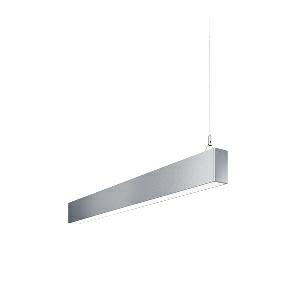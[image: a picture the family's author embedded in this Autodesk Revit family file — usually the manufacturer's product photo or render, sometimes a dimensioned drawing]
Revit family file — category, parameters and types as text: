
# Revit family: dotoo_line_-_dlp_1000_830_d_end_00805842_5508
name_source: partatom
category: Lighting Fixtures
units: mm (PartAtom-declared; Revit-internal decimal feet)

## family parameters
Cut with Voids When Loaded = No
Host = Face
Light Source = No
Part Type = Normal
Room Calculation Point = No
Round Connector Dimension = Use Diameter
Shared = No

## types (1)
- DOTOO.line - DLP 1000/830/D END (1 x LED, 1000 lm, 3000K)
    Apparent Load = 10 VA
    Approval mark = CE
    CIE Flux Codes = 67 91 98 100 100
    Color Rendering = 80-89
    Color Temperature = 3000K
    Control Gear = Electronic ballast
    Default Elevation = 1800 mm
    Description = DLP 1000/830/D|Suspended luminaire|light source: LED|connected load: 220-240 V, 50/60 Hz|Power consumption: approx. 10 W|standby: approx. 0,20|luminous flux: 1000 lm|luminous efficacy: 100 lm/W|light distribution: Direct|direct ratio: approx. 100 %|colour temperature: Warm white, ca. 3000 K|color rendering index (CRI): >= 80|chromaticity tolerance:  3 SDCM|System of protection: IP 40|technology: Continuously dimmable|luminaire body|material: Sectional aluminium|colour: Silver|lamp cover: Acrylic (PMMA), Clear|mains lead: 1,0 m With free stranded wires|Fastening: Steel cable 0.3 - 0.7 m|glare control: Prism aperture|luminance(L65): <= 3000 cd/m|unified glare rating(4H 8H): <=  19|special features: DALI Load 1x, TouchDIM - dimming via standard switch, Through-wired, up to 18 m on one mains connection, Flicker-free, Suitable as emergency lighting, Mechanical and electrical connection of the individual modules without tools|
    Frequency = 50 Hz
    Height = 110 mm
    Lamp = 1 x LED
    Lamp Light Flux = 1000 lm
    Lamp count = 1
    Length = 848 mm
    Luminous efficacy = 100 lm/W
    Manufacturer = Waldmann
    ModVariant = No
    Model = 00805842
    Mounting Place = Ceiling
    Mounting Type = Pendant
    Number of Poles = 1
    OnlyDefault = Yes
    Power Factor = 1
    Product Name = DOTOO.line - DLP 1000/830/D END
    Product group = Suspended luminaire
    ProductGroupID = 9
    Protection Class = Protection class I
    Protection Degree = IP 40
    RLX_Detail_Level = 1
    RLX_Emergency_Light_Flux = 0 lm
    RLX_Emergency_Type = 0
    RLX_Emergency_Type_DB = No
    RlxData = <blob elided: 18713 chars, md5=a484e0ee>
    Socket = socket
    Standby Power = 0 W
    System Light Flux = 1000 lm
    System Power = 10 W
    Type Comments = Product without accessories
    Type Image = 113300000-00692564.jpg
    URL = http://relux.com
    VarID = ---
    Voltage = 230 V
    Voltage Range = 220-240 V
    Weight = 0.00 kg
    Width = 60 mm  [stored 0.19685 ft]

note: [stored X ft] marks values corroborated as IEEE doubles in the binary element streams (Revit-internal decimal feet)

## geometry (parser evidence)
native form markers: Blend x4, Sweep x11
no freeform markers — native parametric forms only
